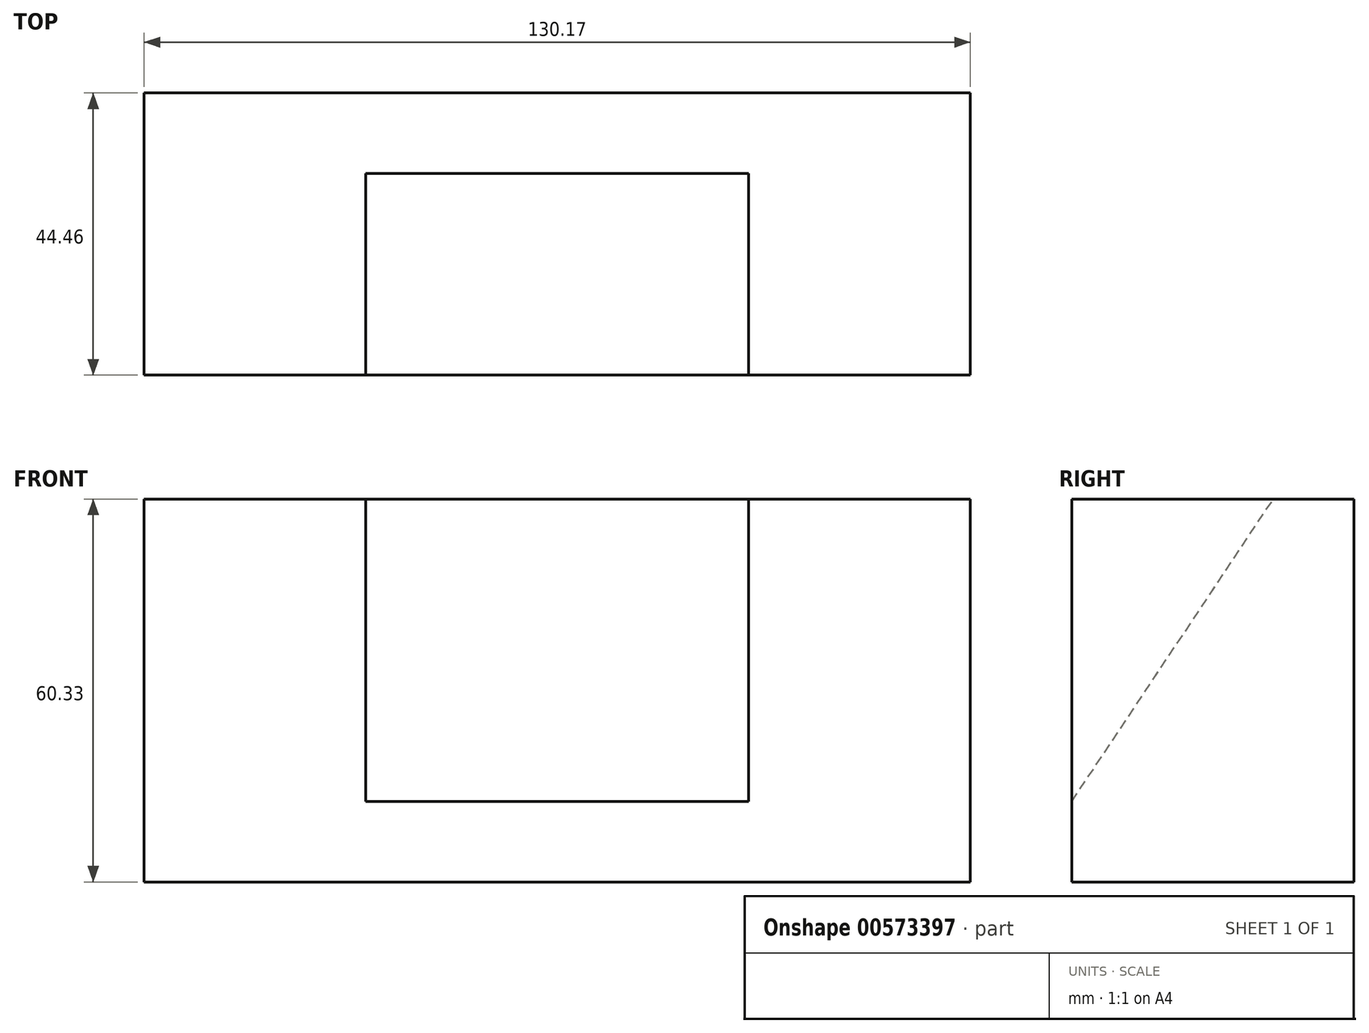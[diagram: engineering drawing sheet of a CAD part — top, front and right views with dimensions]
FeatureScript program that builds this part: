
annotation { "Feature Type Name" : "Feature", "Feature Type Description" : "" }
export const myFeature = defineFeature(function(context is Context, id is Id, definition is map)
    precondition{}
    {
        {
            var Q0;
            Q0=qCreatedBy(makeId("Front.planeOp"),FACE);
            var sketch = newSketch(context, id + "F0", { "sketchPlane" : qUnion([Q0])});
            skLineSegment(sketch, "E0", {"start": v(-64.34, -60.33) * mm, "end": v(-29.42, -60.33) * mm});
            skLineSegment(sketch, "E1", {"start": v(-29.42, -60.33) * mm, "end": v(-29.42, 0) * mm});
            skLineSegment(sketch, "E2", {"start": v(-29.42, 0) * mm, "end": v(-64.34, 0) * mm});
            skLineSegment(sketch, "E3", {"start": v(-64.34, 0) * mm, "end": v(-64.34, -60.33) * mm});
            skSolve(sketch);
        }
        {
            var Q0;
            Q0=makeQuery(id+"F0.imprint","IMPRINT",FACE,{"disambiguationData":[TD([[makeQuery(id+"F0.imprint","IMPRINT",EDGE,{"derivedFrom":sQuery(id+"F0.wireOp",EDGE,"E0")}),1.0]])]});
            extrude(context, id + "F1", {"entities" : qUnion([Q0]), "depth" : 44.45 * mm, "offsetDistance" : 25.4 * mm});
        }
        {
            var Q0;
            Q0=makeQuery(id+"F1.opExtrude","SWEPT_FACE",FACE,{"disambiguationData":[OSD([sQuery(id+"F0.wireOp",EDGE,"E1")])]});
            var sketch = newSketch(context, id + "F2", { "sketchPlane" : qUnion([Q0])});
            skLineSegment(sketch, "E4", {"start": v(-44.45, -60.33) * mm, "end": v(-44.45, -47.63) * mm});
            skLineSegment(sketch, "E5", {"start": v(0, -60.33) * mm, "end": v(-44.45, -60.33) * mm});
            skPoint(sketch, "E6.end.orphan", {"position": v(0, -47.63) * mm});
            skLineSegment(sketch, "E7", {"start": v(0, -47.63) * mm, "end": v(0, -60.33) * mm});
            skLineSegment(sketch, "E8", {"start": v(-44.45, -47.63) * mm, "end": v(-12.7, 0) * mm});
            skLineSegment(sketch, "E9", {"start": v(-12.7, 0) * mm, "end": v(0, 0) * mm});
            skLineSegment(sketch, "E10", {"start": v(0, 0) * mm, "end": v(0, -60.33) * mm});
            skSolve(sketch);
        }
        {
            var Q0;
            Q0=makeQuery(id+"F2.imprint","IMPRINT",FACE,{"disambiguationData":[TD([[makeQuery(id+"F2.imprint","IMPRINT",EDGE,{"derivedFrom":sQuery(id+"F2.wireOp",EDGE,"E4")}),-1.0]])]});
            extrude(context, id + "F3", {"entities" : qUnion([Q0]), "operationType" : NewBodyOperationType.ADD, "depth" : 60.32 * mm, "offsetDistance" : 25.4 * mm});
        }
        {
            var Q0;
            Q0=makeQuery(id+"F3.opExtrude","CAP_FACE",FACE,{"disambiguationData":[OSD([sQuery(id+"F2.wireOp",EDGE,"E4"),sQuery(id+"F2.wireOp",EDGE,"E5"),sQuery(id+"F2.wireOp",EDGE,"E8"),sQuery(id+"F2.wireOp",EDGE,"E9"),sQuery(id+"F2.wireOp",EDGE,"E10")])],"isStart":false});
            var sketch = newSketch(context, id + "F4", { "sketchPlane" : qUnion([Q0])});
            skLineSegment(sketch, "E11", {"start": v(0, 0) * mm, "end": v(-44.46, 0) * mm});
            skLineSegment(sketch, "E12", {"start": v(-44.46, 0) * mm, "end": v(-44.45, -60.33) * mm});
            skLineSegment(sketch, "E13", {"start": v(-44.45, -60.33) * mm, "end": v(0, -60.33) * mm});
            skLineSegment(sketch, "E14", {"start": v(0, -60.33) * mm, "end": v(0, 0) * mm});
            skLineSegment(sketch, "E15", {"start": v(-44.45, -47.63) * mm, "end": v(-12.7, 0) * mm});
            skSolve(sketch);
        }
        {
            var Q0;
            {var subQ2=sQuery(id+"F4.wireOp",EDGE,"E12");Q0=makeQuery(id+"F4.imprint","IMPRINT",FACE,{"disambiguationData":[TD([[makeQuery(id+"F4.imprint","IMPRINT",EDGE,{"derivedFrom":subQ2}),1.0]])]});}
            var Q1;
            Q1=makeQuery(id+"F4.imprint","IMPRINT",FACE,{"disambiguationData":[TD([[makeQuery(id+"F4.imprint","IMPRINT",EDGE,{"derivedFrom":sQuery(id+"F4.wireOp",EDGE,"E13")}),1.0]])]});
            extrude(context, id + "F5", {"entities" : qUnion([Q0, Q1]), "operationType" : NewBodyOperationType.ADD, "depth" : 34.92 * mm, "offsetDistance" : 25.4 * mm});
        }
    });
